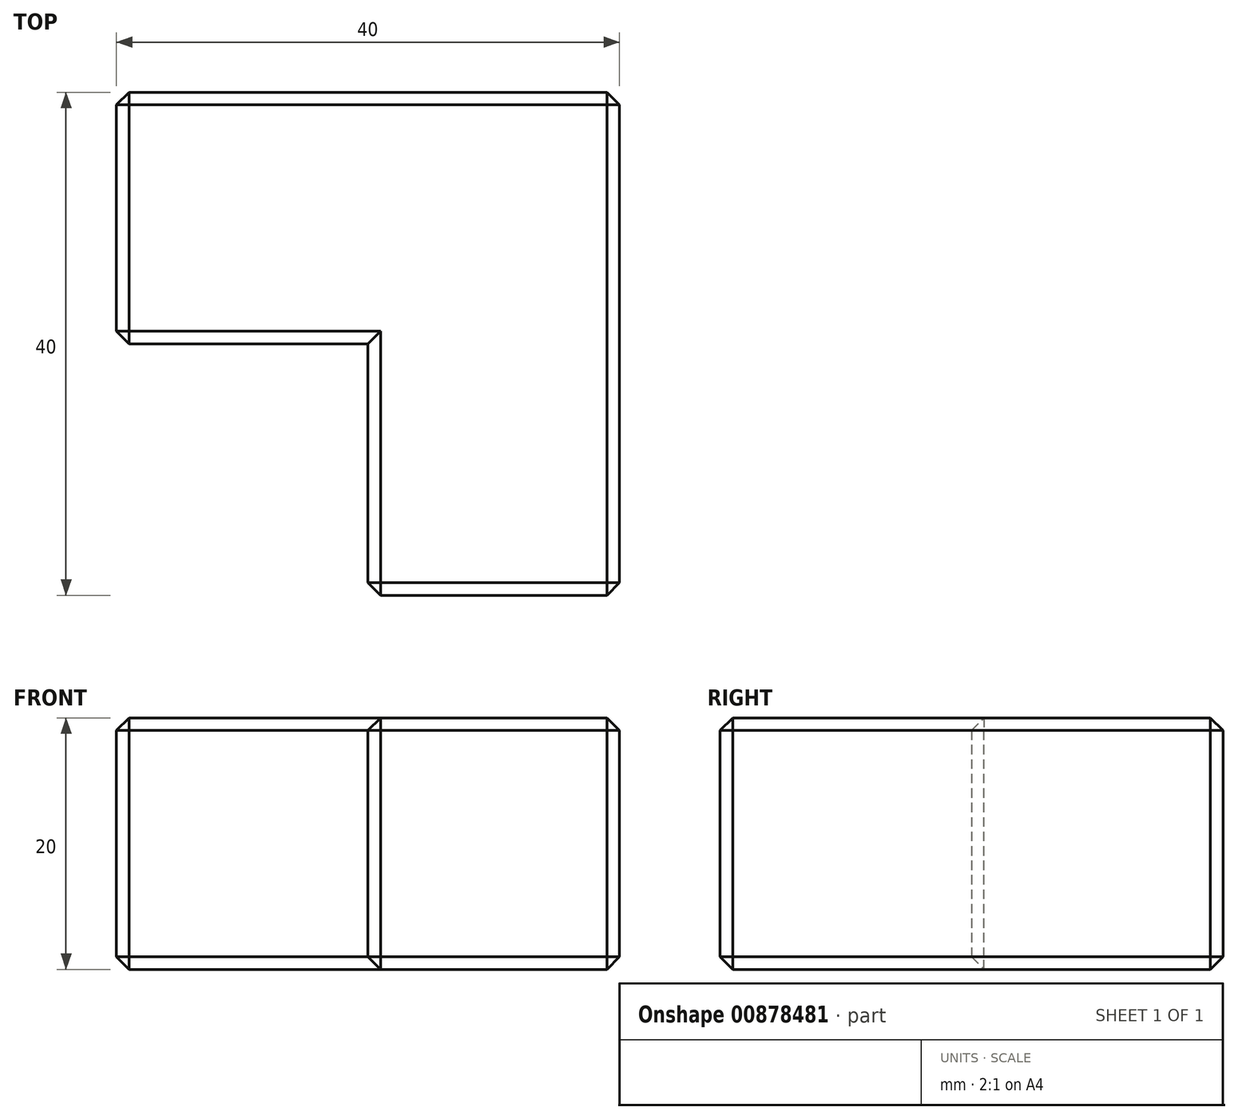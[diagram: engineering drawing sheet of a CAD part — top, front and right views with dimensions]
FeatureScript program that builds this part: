
annotation { "Feature Type Name" : "Feature", "Feature Type Description" : "" }
export const myFeature = defineFeature(function(context is Context, id is Id, definition is map)
    precondition{}
    {
        {
            var Q0;
            Q0=qCreatedBy(makeId("Top.planeOp"),FACE);
            var sketch = newSketch(context, id + "F0", { "sketchPlane" : qUnion([Q0])});
            skLineSegment(sketch, "E0.bottom", {"start": v(-19.33, 19.57) * mm, "end": v(20.67, 19.57) * mm});
            skLineSegment(sketch, "E0.top", {"start": v(0.67, -20.43) * mm, "end": v(20.67, -20.43) * mm});
            skLineSegment(sketch, "E0.left", {"start": v(-19.33, 19.57) * mm, "end": v(-19.33, -0.43) * mm});
            skLineSegment(sketch, "E0.right", {"start": v(20.67, 19.57) * mm, "end": v(20.67, -20.43) * mm});
            skLineSegment(sketch, "E1.bottom", {"start": v(-19.33, -0.43) * mm, "end": v(0.67, -0.43) * mm});
            skLineSegment(sketch, "E1.right", {"start": v(0.67, -0.43) * mm, "end": v(0.67, -20.43) * mm});
            skPoint(sketch, "E2.orphan", {"position": v(-19.33, -20.43) * mm});
            skSolve(sketch);
        }
        {
            var Q0;
            Q0=makeQuery(id+"F0.imprint","IMPRINT",FACE,{"disambiguationData":[TD([[makeQuery(id+"F0.imprint","IMPRINT",EDGE,{"derivedFrom":sQuery(id+"F0.wireOp",EDGE,"E0.bottom")}),-1.0]])]});
            extrude(context, id + "F1", {"entities" : qUnion([Q0]), "depth" : 20 * mm, "offsetDistance" : 25 * mm});
        }
        {
            var Q0;
            Q0=makeQuery(id+"F1.opExtrude","SWEPT_FACE",FACE,{"disambiguationData":[OSD([sQuery(id+"F0.wireOp",EDGE,"E0.top")])]});
            var Q1;
            Q1=makeQuery(id+"F1.opExtrude","SWEPT_FACE",FACE,{"disambiguationData":[OSD([sQuery(id+"F0.wireOp",EDGE,"E0.left")])]});
            var Q2;
            Q2=makeQuery(id+"F1.opExtrude","CAP_FACE",FACE,{"disambiguationData":[OSD([sQuery(id+"F0.wireOp",EDGE,"E0.bottom"),sQuery(id+"F0.wireOp",EDGE,"E0.top"),sQuery(id+"F0.wireOp",EDGE,"E0.left"),sQuery(id+"F0.wireOp",EDGE,"E0.right"),sQuery(id+"F0.wireOp",EDGE,"E1.bottom"),sQuery(id+"F0.wireOp",EDGE,"E1.right")])],"isStart":true});
            var Q3;
            Q3=makeQuery(id+"F1.opExtrude","SWEPT_FACE",FACE,{"disambiguationData":[OSD([sQuery(id+"F0.wireOp",EDGE,"E0.right")])]});
            var Q4;
            Q4=makeQuery(id+"F1.opExtrude","SWEPT_FACE",FACE,{"disambiguationData":[OSD([sQuery(id+"F0.wireOp",EDGE,"E0.bottom")])]});
            var Q5;
            Q5=makeQuery(id+"F1.opExtrude","CAP_FACE",FACE,{"disambiguationData":[OSD([sQuery(id+"F0.wireOp",EDGE,"E0.bottom"),sQuery(id+"F0.wireOp",EDGE,"E0.top"),sQuery(id+"F0.wireOp",EDGE,"E0.left"),sQuery(id+"F0.wireOp",EDGE,"E0.right"),sQuery(id+"F0.wireOp",EDGE,"E1.bottom"),sQuery(id+"F0.wireOp",EDGE,"E1.right")])],"isStart":false});
            chamfer(context, id + "F2", {"entities" : qUnion([Q0, Q1, Q2, Q3, Q4, Q5]), "width" : 1 * mm, "tangentPropagation" : true});
        }
    });
